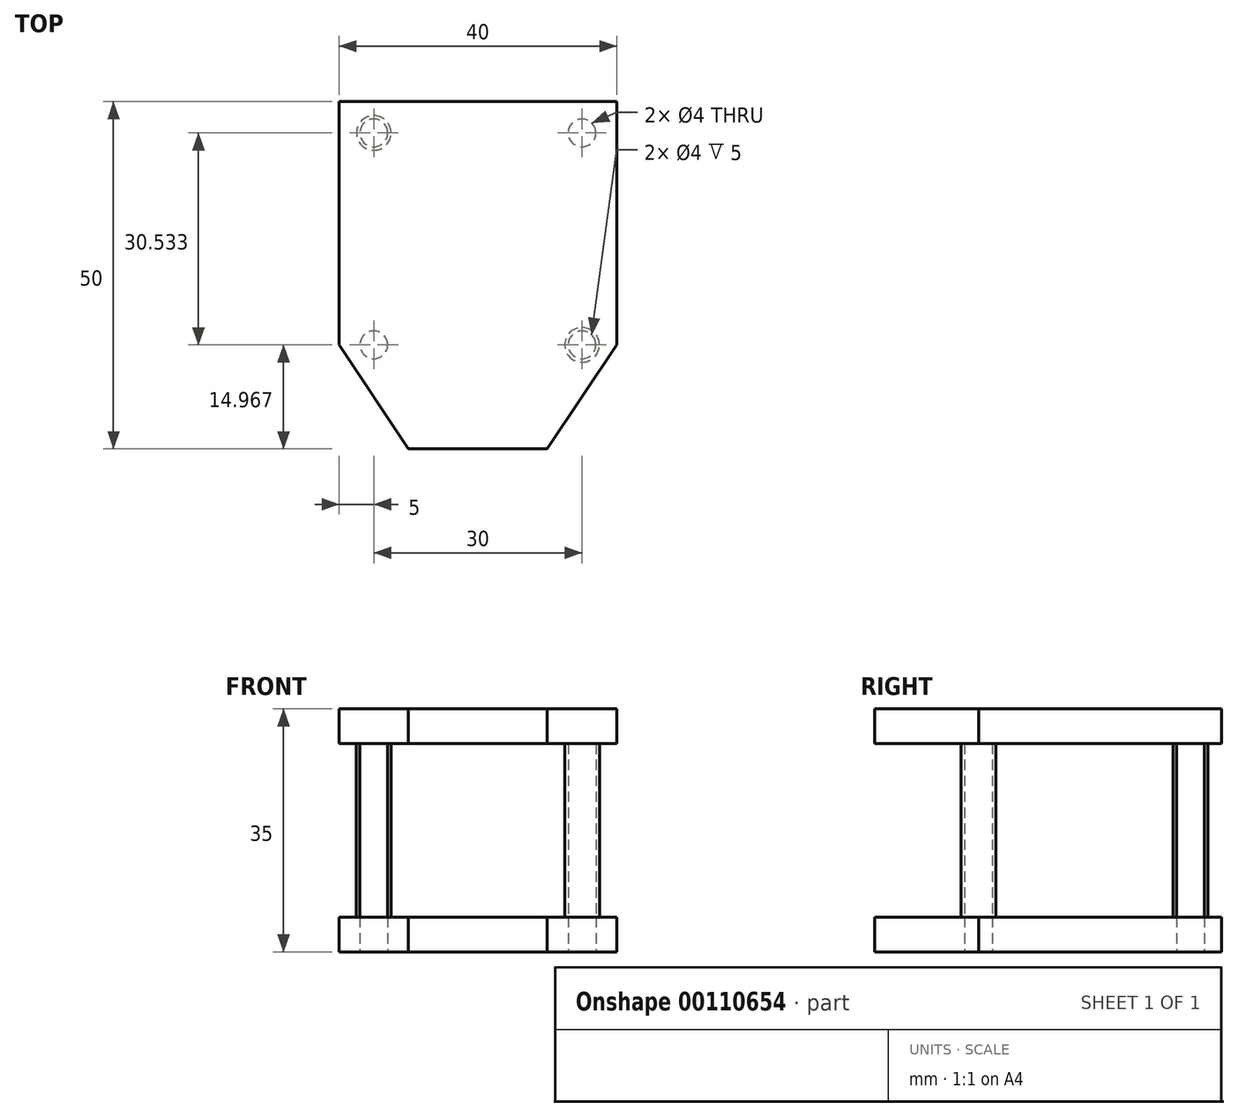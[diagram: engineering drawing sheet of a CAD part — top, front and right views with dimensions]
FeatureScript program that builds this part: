
annotation { "Feature Type Name" : "Feature", "Feature Type Description" : "" }
export const myFeature = defineFeature(function(context is Context, id is Id, definition is map)
    precondition{}
    {
        {
            var Q0;
            Q0=qCreatedBy(makeId("Top.planeOp"),FACE);
            var sketch = newSketch(context, id + "F0", { "sketchPlane" : qUnion([Q0])});
            skLineSegment(sketch, "E0", {"start": v(-10, 38.3) * mm, "end": v(30, 38.3) * mm});
            skLineSegment(sketch, "E1", {"start": v(30, 38.3) * mm, "end": v(30, 3.26) * mm});
            skLineSegment(sketch, "E2", {"start": v(30, 3.26) * mm, "end": v(20, -11.7) * mm});
            skLineSegment(sketch, "E3", {"start": v(20, -11.7) * mm, "end": v(0, -11.7) * mm});
            skLineSegment(sketch, "E4", {"start": v(0, -11.7) * mm, "end": v(-10, 3.26) * mm});
            skLineSegment(sketch, "E5", {"start": v(-10, 3.26) * mm, "end": v(-10, 38.3) * mm});
            skCircle(sketch, "E6", {"center": v(-5, 33.8) * mm, "radius": 2 * mm});
            skCircle(sketch, "E7", {"center": v(25, 33.8) * mm, "radius": 2 * mm});
            skCircle(sketch, "E8", {"center": v(-5, 3.26) * mm, "radius": 2 * mm});
            skPoint(sketch, "E8.centerSnap0", {"position": v(-5, -4.23) * mm});
            skCircle(sketch, "E9", {"center": v(25, 3.26) * mm, "radius": 2 * mm});
            skSolve(sketch);
        }
        {
            var Q0;
            Q0 = qSketchRegion(id + "F0", true);
            extrude(context, id + "F1", {"entities" : qUnion([Q0]), "depth" : 5 * mm});
        }
        {
            var Q0;
            Q0=makeQuery(id+"F1.opExtrude","CAP_FACE",FACE,{"disambiguationData":[OSD([sQuery(id+"F0.wireOp",EDGE,"E0"),sQuery(id+"F0.wireOp",EDGE,"E1"),sQuery(id+"F0.wireOp",EDGE,"E2"),sQuery(id+"F0.wireOp",EDGE,"E3"),sQuery(id+"F0.wireOp",EDGE,"E4"),sQuery(id+"F0.wireOp",EDGE,"E5"),sQuery(id+"F0.wireOp",EDGE,"E6"),sQuery(id+"F0.wireOp",EDGE,"E7"),sQuery(id+"F0.wireOp",EDGE,"E8"),sQuery(id+"F0.wireOp",EDGE,"E9")])],"isStart":false});
            var sketch = newSketch(context, id + "F2", { "sketchPlane" : qUnion([Q0])});
            skCircle(sketch, "E10.0", {"center": v(-5, 33.8) * mm, "radius": 2 * mm});
            skCircle(sketch, "E11.0", {"center": v(25, 33.8) * mm, "radius": 2 * mm});
            skCircle(sketch, "E12.0", {"center": v(25, 3.26) * mm, "radius": 2 * mm});
            skCircle(sketch, "E13.0", {"center": v(-5, 3.26) * mm, "radius": 2 * mm});
            skCircle(sketch, "E14", {"center": v(-5, 33.8) * mm, "radius": 2.5 * mm});
            skCircle(sketch, "E15", {"center": v(25, 33.8) * mm, "radius": 2.5 * mm});
            skCircle(sketch, "E16", {"center": v(-5, 3.26) * mm, "radius": 2.5 * mm});
            skCircle(sketch, "E17", {"center": v(25, 3.26) * mm, "radius": 2.5 * mm});
            skSolve(sketch);
        }
        {
            var Q0;
            Q0=makeQuery(id+"F2.imprint","IMPRINT",FACE,{"disambiguationData":[TD([[makeQuery(id+"F2.imprint","IMPRINT",EDGE,{"derivedFrom":makeQuery(id+"F1.opExtrude","CAP_EDGE",EDGE,{"disambiguationData":[OSD([sQuery(id+"F0.wireOp",EDGE,"E0")])],"isStart":false})}),-1.0]])]});
            var sketch = newSketch(context, id + "F3", { "sketchPlane" : qUnion([Q0])});
            skSolve(sketch);
        }
        {
            var Q0;
            Q0=makeQuery(id+"F2.imprint","IMPRINT",FACE,{"disambiguationData":[TD([[makeQuery(id+"F2.imprint","IMPRINT",EDGE,{"derivedFrom":sQuery(id+"F2.wireOp",EDGE,"E10.0")}),1.0]])]});
            var Q1;
            Q1=makeQuery(id+"F2.imprint","IMPRINT",FACE,{"disambiguationData":[TD([[makeQuery(id+"F2.imprint","IMPRINT",EDGE,{"derivedFrom":sQuery(id+"F2.wireOp",EDGE,"E10.0")}),-1.0]])]});
            var Q2;
            Q2=makeQuery(id+"F3.imprint","IMPRINT",FACE,{"disambiguationData":[TD([[makeQuery(id+"F3.imprint","IMPRINT",EDGE,{"derivedFrom":makeQuery(id+"F2.imprint","IMPRINT",EDGE,{"derivedFrom":sQuery(id+"F2.wireOp",EDGE,"E15")})}),1.0]])]});
            var Q3;
            Q3=makeQuery(id+"F2.imprint","IMPRINT",FACE,{"disambiguationData":[TD([[makeQuery(id+"F2.imprint","IMPRINT",EDGE,{"derivedFrom":sQuery(id+"F2.wireOp",EDGE,"E11.0")}),1.0]])]});
            var Q4;
            Q4=makeQuery(id+"F2.imprint","IMPRINT",FACE,{"disambiguationData":[TD([[makeQuery(id+"F2.imprint","IMPRINT",EDGE,{"derivedFrom":sQuery(id+"F2.wireOp",EDGE,"E12.0")}),1.0]])]});
            var Q5;
            Q5=makeQuery(id+"F2.imprint","IMPRINT",FACE,{"disambiguationData":[TD([[makeQuery(id+"F2.imprint","IMPRINT",EDGE,{"derivedFrom":sQuery(id+"F2.wireOp",EDGE,"E12.0")}),-1.0]])]});
            var Q6;
            Q6=makeQuery(id+"F2.imprint","IMPRINT",FACE,{"disambiguationData":[TD([[makeQuery(id+"F2.imprint","IMPRINT",EDGE,{"derivedFrom":sQuery(id+"F2.wireOp",EDGE,"E13.0")}),1.0]])]});
            var Q7;
            Q7=makeQuery(id+"F3.imprint","IMPRINT",FACE,{"disambiguationData":[TD([[makeQuery(id+"F3.imprint","IMPRINT",EDGE,{"derivedFrom":makeQuery(id+"F2.imprint","IMPRINT",EDGE,{"derivedFrom":sQuery(id+"F2.wireOp",EDGE,"E16")})}),1.0]])]});
            extrude(context, id + "F4", {"entities" : qUnion([Q0, Q1, Q2, Q3, Q4, Q5, Q6, Q7]), "operationType" : NewBodyOperationType.ADD, "depth" : 25 * mm});
        }
        {
            var Q0;
            Q0=makeQuery(id+"F4.opExtrude","CAP_FACE",FACE,{"disambiguationData":[OSD([sQuery(id+"F2.wireOp",EDGE,"E14")])],"isStart":false});
            var sketch = newSketch(context, id + "F5", { "sketchPlane" : qUnion([Q0])});
            skLineSegment(sketch, "E18.0", {"start": v(-10, 38.3) * mm, "end": v(30, 38.3) * mm});
            skLineSegment(sketch, "E18.1", {"start": v(-10, 3.26) * mm, "end": v(-10, 38.3) * mm});
            skLineSegment(sketch, "E18.2", {"start": v(20, -11.7) * mm, "end": v(0, -11.7) * mm});
            skLineSegment(sketch, "E18.3", {"start": v(0, -11.7) * mm, "end": v(-10, 3.26) * mm});
            skLineSegment(sketch, "E18.4", {"start": v(30, 3.26) * mm, "end": v(20, -11.7) * mm});
            skLineSegment(sketch, "E18.5", {"start": v(30, 38.3) * mm, "end": v(30, 3.26) * mm});
            skSolve(sketch);
        }
        {
            var Q0;
            Q0 = qSketchRegion(id + "F5", true);
            extrude(context, id + "F6", {"entities" : qUnion([Q0]), "depth" : 5 * mm});
        }
    });
